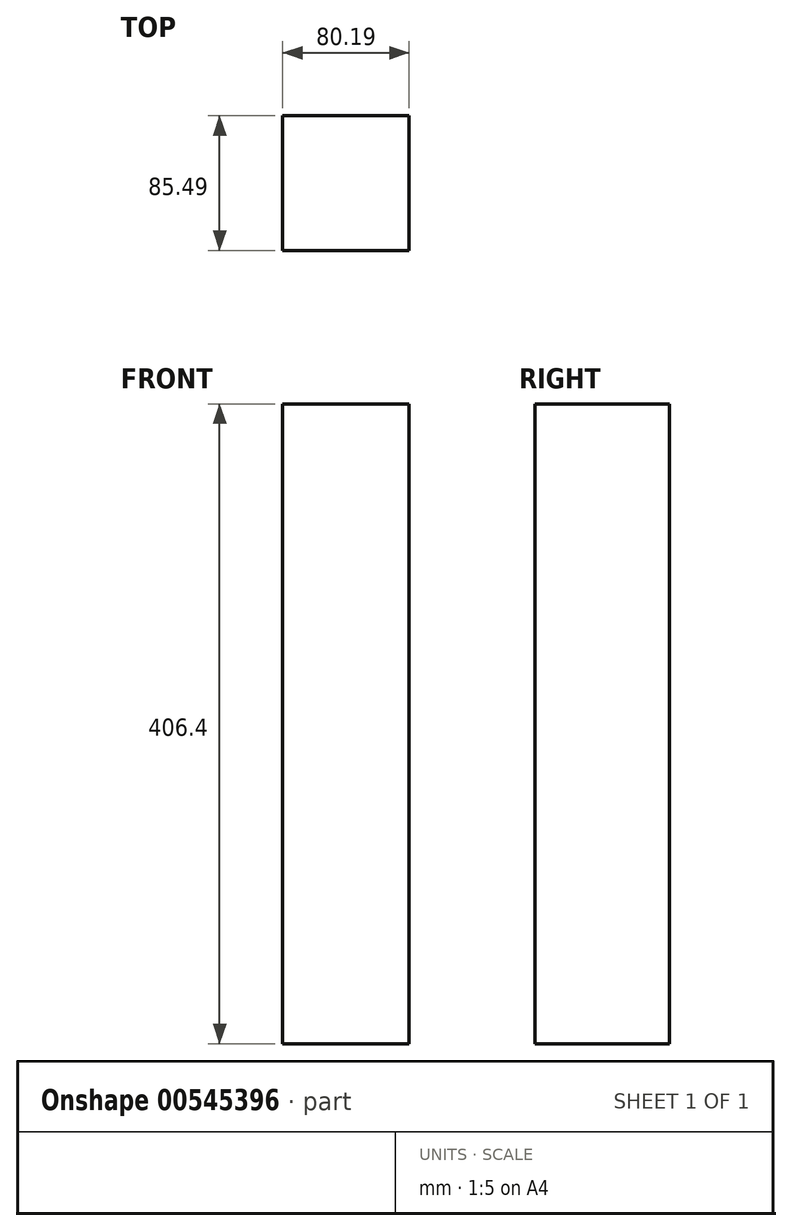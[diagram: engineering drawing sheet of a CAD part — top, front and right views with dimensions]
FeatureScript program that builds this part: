
annotation { "Feature Type Name" : "Feature", "Feature Type Description" : "" }
export const myFeature = defineFeature(function(context is Context, id is Id, definition is map)
    precondition{}
    {
        {
            var Q0;
            Q0=qCreatedBy(makeId("Top.planeOp"),FACE);
            var sketch = newSketch(context, id + "F0", { "sketchPlane" : qUnion([Q0])});
            skLineSegment(sketch, "E0.bottom", {"start": v(38.83, 41.1) * mm, "end": v(-41.36, 41.1) * mm});
            skLineSegment(sketch, "E0.top", {"start": v(38.83, -44.4) * mm, "end": v(-41.36, -44.4) * mm});
            skLineSegment(sketch, "E0.left", {"start": v(38.83, 41.1) * mm, "end": v(38.83, -44.4) * mm});
            skLineSegment(sketch, "E0.right", {"start": v(-41.36, 41.1) * mm, "end": v(-41.36, -44.4) * mm});
            skSolve(sketch);
        }
        {
            var Q0;
            Q0 = qSketchRegion(id + "F0", true);
            extrude(context, id + "F1", {"entities" : qUnion([Q0]), "depth" : 406.4 * mm, "offsetDistance" : 25.4 * mm});
        }
    });
